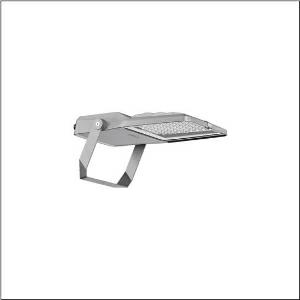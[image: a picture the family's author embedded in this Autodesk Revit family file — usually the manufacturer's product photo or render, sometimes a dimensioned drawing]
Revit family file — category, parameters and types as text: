
# Revit family: floodlight_fl_21_iq_mini___pl52_5xa7772b1d1a_732a
name_source: partatom
category: Lighting Fixtures
units: mm (PartAtom-declared; Revit-internal decimal feet)

## family parameters
Cut with Voids When Loaded = No
Host = Face
Light Source = No
Part Type = Normal
Room Calculation Point = No
Round Connector Dimension = Use Diameter
Shared = No

## types (1)
- --- (1 x LED, 5170 lm, 45.5 W, 2200K)
    Apparent Load = 46 VA
    CIE Flux Codes = 26 60 98 100 100
    Color Rendering = 70
    Color Temperature = 2200K
    Default Elevation = 1800 mm
    Description = Floodlight FL 21 iQ mini, floodlight, primary light control with lens, of PMMA, primary optical cover: protective disc, of toughened safety glass, transparent, light distribution: PL52, light emission: direct distribution, installation type: surface-mounted, lamps: LED, High Power LED, rated values: 5.170lm | 45,5W | 113,6lm/W (begin service life); end service life: 5.170lm | 48W; at 50% lumin. flux: 2.585lm | 21,4W | 120,8lm/W, colour temperature: 2200K, colour rendering: CRI > 70, light colour: 722, light setting 1 begin service life: 100% | 5.170lm | 45,5W | 113,6lm/W | 2.200K, light setting 1 end service life: 48W, further light settings possible, control: Street-Remote, Auto-Match, Temp-Guard, Night-Set, Smart-Wire, Desk-Remote (wireless, voltage-free reading and setting of iQ features in the workshop via application-optimized NFC function/RFID function), optimised constant luminous flux control (CLO 2.0), pre-setting: linear dimming characteristic, with terminal, 6-pole, mains connection: 220..240V, AC, 50/60Hz, luminaire housing, of diecast aluminium, powder-coated, SITECO metallic grey (DB 702S), corrosivity category C5 mid according to DIN EN ISO 12944suitable for swimming poolschlorine-resistant, sealing non-destructively replaceable, mounting bracket, of steel, galvanised, powder-coated, SITECO metallic grey (DB 702S), protection rating (complete): IP66, insulation class (complete): insulation class II (safety insulation), certification: CE, ENEC, VDE, protection symbol: D, impact resistance: IK08, permissible operating ambient temperature: -40..+40°C, permissible operating ambient temperature for outdoor applications: -40..+50°C, standard: DIN EN 12944, LABS conformity tested according to VDMA 24364:2018-05, packaging unit: 1 piece

Light Distribution: PL52
    Height = 70 mm
    Lamp = 1 x LED
    Lamp Light Flux = 5170 lm
    Lamp Power = 45.5 W
    Lamp count = 1
    Length = 485 mm
    Luminous efficacy = 114 lm/W
    Manufacturer = Siteco
    ModVariant = No
    Model = 5XA7772B1D1A
    Number of Poles = 1
    OnlyDefault = Yes
    Power Factor = 1
    Product Name = Floodlight FL 21 iQ mini | PL52
    Product group = floodlight | pylon annexe
    ProductGroupID = 6201
    Protection Class = Protection class II
    Protection Degree = IP 66
    RLX_Detail_Level = 1
    RLX_Emergency_Light_Flux = 0 lm
    RLX_Emergency_Type = 0
    RLX_Emergency_Type_DB = No
    RlxData = <blob elided: 96609 chars, md5=8d0a86bf>
    Socket = socket
    Standby Power = 0 W
    System Light Flux = 5170 lm
    System Power = 46 W
    Type Comments = factory setting: luminous flux: 100 % | dim-lin: 254 | 463 mA
    Type Image = l_1006845.jpg
    URL = http://relux.com
    VarID = @adj_164421
    Voltage = 0 V
    Weight = 0.00 kg
    Width = 337 mm

## geometry (parser evidence)
native form markers: Blend x4, Sweep x12
no freeform markers — native parametric forms only
